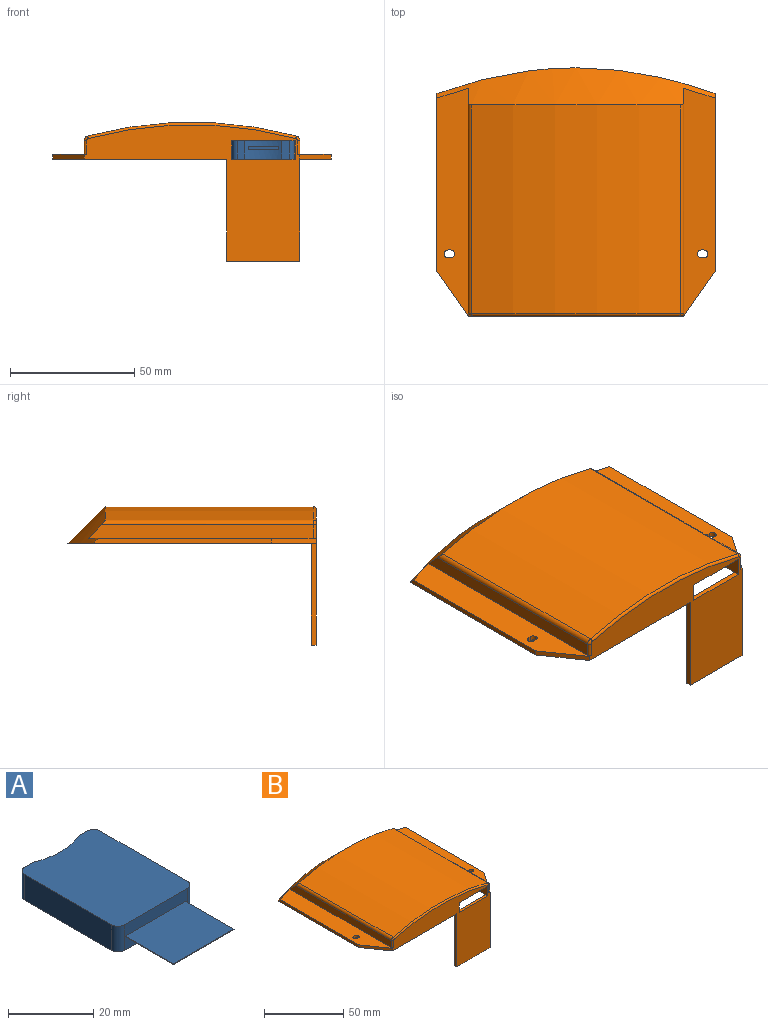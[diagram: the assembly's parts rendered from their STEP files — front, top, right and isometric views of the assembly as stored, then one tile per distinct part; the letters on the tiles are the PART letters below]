
ASSEMBLY  parts=2 mates=1
PART A: 24 faces, bbox 25x49x7.4 mm
  f0: plane 10x1.4mm, normal (1,0,0), area 13.8mm2, adj f5,f14,f15,f16,f17,f18
  f1: plane 10x1.4mm, normal (-1,0,0), area 13.8mm2, adj f5,f14,f15,f16,f17,f18
  f2: plane 29x7.35mm, normal (1,0,0), area 213.2mm2, adj f3,f11,f12,f13
  f3: cylinder r=2mm len=7.35mm, axis (0,0,-1), area 23.1mm2, adj f2,f4,f12,f13
  f4: plane 7.35x3mm, normal (0,1,0), area 22.1mm2, adj f3,f5,f12,f13
  f5: cylinder r=19.5mm len=15mm, axis (0,0,-1), area 96.1mm2, adj f0,f1,f4,f6,f12,f13,f15,f16
  f6: plane 7.35x3mm, normal (0,1,0), area 22.1mm2, adj f5,f7,f12,f13
  f7: cylinder r=2mm len=7.35mm, axis (0,0,-1), area 23.1mm2, adj f6,f8,f12,f13
  f8: plane 29x7.35mm, normal (-1,0,0), area 213.2mm2, adj f7,f9,f12,f13
  f9: cylinder r=2mm len=7.35mm, axis (0,0,-1), area 23.1mm2, adj f8,f10,f12,f13
  f10: plane 21x7.35mm, normal (0,-1,0), area 150.3mm2, adj f9,f11,f12,f13,f19,f20,f21,f23
  f11: cylinder r=2mm len=7.35mm, axis (0,0,-1), area 23.1mm2, adj f2,f10,f12,f13
  f12: plane 33x25mm, normal (0,0,1), area 806.4mm2, adj f2,f3,f4,f5,f6,f7,f8,f9
  f13: plane 33x25mm, normal (0,0,-1), area 806.4mm2, adj f2,f3,f4,f5,f6,f7,f8,f9
  f14: plane 12x1.2mm, normal (0,1,0), area 14.4mm2, adj f0,f1,f15,f17
  f15: plane 12x10mm, normal (0,0,-1), area 112.3mm2, adj f0,f1,f5,f14
  f16: plane 12x9mm, normal (0,0,1), area 100.3mm2, adj f0,f1,f5,f18
  f17: plane 12x1mm, normal (0,0,1), area 12mm2, adj f0,f1,f14,f18
  f18: plane 12x0.2mm, normal (0,1,0), area 2.4mm2, adj f0,f1,f16,f17
  f19: plane 20x15.95mm, normal (0,0,1), area 319.1mm2, adj f10,f20,f21,f22
  f20: plane 15.95x0.2mm, normal (1,0,0), area 3.2mm2, adj f10,f19,f22,f23
  f21: plane 15.95x0.2mm, normal (-1,0,0), area 3.2mm2, adj f10,f19,f22,f23
  f22: plane 20x0.2mm, normal (0,-1,0), area 4mm2, adj f19,f20,f21,f23
  f23: plane 20x15.95mm, normal (0,0,-1), area 319.1mm2, adj f10,f20,f21,f22
PART B: 47 faces, bbox 115.4x100x69.3 mm
  f0: plane 112x100mm, normal (0,0,-1), area 2767mm2, adj f2,f3,f4,f8,f9,f13,f14,f16
  f1: plane 28x3.75mm, normal (0,0,-1), area 59.5mm2, adj f2,f3,f15,f31,f39,f46
  f2: plane 25.5x7.5mm, normal (0,-1,0), area 103.2mm2, adj f0,f1,f15,f16,f17,f39,f40,f41
  f3: plane 27.5x12.38mm, normal (0,1,0), area 196.8mm2, adj f0,f1,f5,f28,f31,f39,f40,f41
  f4: plane 55.5x13mm, normal (0,1,0), area 643.1mm2, adj f0,f5,f29,f31
  f5: cylinder r=159.32mm len=83mm, axis (0,1,0), area 6116.8mm2, adj f3,f4,f28,f29,f30,f31
  f6: plane 91.75x13.5mm, normal (0,0,1), area 999.5mm2, adj f8,f9,f10,f14,f23,f24,f25,f26
  f7: plane 91.75x13.5mm, normal (0,0,1), area 999.5mm2, adj f8,f12,f13,f14,f18,f19,f20,f21
  f8: plane 87x55mm, normal (0,-1,0), area 2050.7mm2, adj f0,f6,f7,f15,f16,f17,f22,f23
  f9: plane 71.65x2mm, normal (1,0,0), area 141.4mm2, adj f0,f6,f14,f23
  f10: plane 90.78x5.53mm, normal (1,0,0), area 484.6mm2, adj f6,f14,f32,f34
  f11: cylinder r=161.32mm len=84.04mm, axis (0,1,0), area 7141.9mm2, adj f14,f32,f33,f36
  f12: plane 90.78x5.53mm, normal (-1,0,0), area 484.6mm2, adj f7,f14,f33,f38
  f13: plane 71.65x2mm, normal (-1,0,0), area 141.4mm2, adj f0,f7,f14,f22
  f14: cone r=161.32mm half-angle=45deg, axis (0,-1,0), area 1671.9mm2, adj f0,f6,f7,f9,f10,f11,f12,f13
  f15: plane 28x7.5mm, normal (1,0,0), area 210mm2, adj f1,f2,f8,f17,f42
  f16: plane 28x7.5mm, normal (-1,0,0), area 210mm2, adj f0,f2,f8,f17,f42
  f17: plane 28x25.5mm, normal (0,0,-1), area 714mm2, adj f2,f8,f15,f16
  f18: plane 2x1mm, normal (0,1,0), area 2mm2, adj f0,f7,f19,f21
  f19: cylinder r=1.6mm len=3.2mm, axis (0,0,-1), area 10.1mm2, adj f0,f7,f18,f20
  f20: plane 2x1mm, normal (0,-1,0), area 2mm2, adj f0,f7,f19,f21
  f21: cylinder r=1.6mm len=3.2mm, axis (0,0,-1), area 10.1mm2, adj f0,f7,f18,f20
  f22: plane 18x12.5mm, normal (-0.82,-0.57,0), area 43.8mm2, adj f0,f7,f8,f13
  f23: plane 18x12.5mm, normal (0.82,-0.57,0), area 43.8mm2, adj f0,f6,f8,f9
  f24: plane 2x1mm, normal (0,-1,0), area 2mm2, adj f0,f6,f25,f27
  f25: cylinder r=1.6mm len=3.2mm, axis (0,0,-1), area 10.1mm2, adj f0,f6,f24,f26
  f26: plane 2x1mm, normal (0,1,0), area 2mm2, adj f0,f6,f25,f27
  f27: cylinder r=1.6mm len=3.2mm, axis (0,0,-1), area 10.1mm2, adj f0,f6,f24,f26
  f28: plane 61.45x7.55mm, normal (-1,0,0), area 433.4mm2, adj f0,f3,f5,f30
  f29: plane 89.45x7.55mm, normal (1,0,0), area 643.4mm2, adj f0,f4,f5,f30
  f30: cone r=159.9mm half-angle=45deg, axis (0,-1,0), area 1312.6mm2, adj f0,f5,f28,f29
  f31: plane 28x12.38mm, normal (-1,0,0), area 346.7mm2, adj f1,f3,f4,f5
  f32: cylinder r=2mm len=85.47mm, axis (0,1,0), area 221mm2, adj f10,f11,f14,f35
  f33: cylinder r=2mm len=85.47mm, axis (0,1,0), area 221mm2, adj f11,f12,f14,f37
  f34: cylinder r=1mm len=5.5mm, axis (0,0,-1), area 8.6mm2, adj f6,f8,f10,f35
  f35: torus R=1mm, axis (0,-1,0), area 3.4mm2, adj f8,f32,f34,f36
  f36: torus R=160.32mm, axis (0,-1,0), area 133.3mm2, adj f8,f11,f35,f37
  f37: torus R=1mm, axis (0,-1,0), area 3.4mm2, adj f8,f33,f36,f38
  f38: cylinder r=1mm len=5.5mm, axis (0,0,1), area 8.6mm2, adj f7,f8,f12,f37
  f39: plane 4x2mm, normal (1,0,0), area 8mm2, adj f1,f2,f3,f41
  f40: plane 4x2mm, normal (-1,0,0), area 8mm2, adj f0,f2,f3,f41
  f41: plane 22x2mm, normal (0,0,-1), area 44mm2, adj f2,f3,f39,f40
  f42: plane 25.5x2mm, normal (0,0,1), area 51mm2, adj f8,f15,f16,f46
  f43: plane 41x2mm, normal (-1,0,0), area 82mm2, adj f0,f8,f44,f46
  f44: plane 29.5x2mm, normal (0,0,-1), area 59mm2, adj f8,f43,f45,f46
  f45: plane 41x2mm, normal (1,0,0), area 82mm2, adj f0,f8,f44,f46
  f46: plane 41x29.5mm, normal (0,1,0), area 1209.5mm2, adj f0,f1,f42,f43,f44,f45
PLACE A rot(axis=(0,0,1),180deg) t=(8.46,-44.75,-3.21)mm
PLACE B t=(-20.29,26.1,-7.03)mm
MATE planar A.f12 <-> B.f17  axis (0,0,1) through (8.46,-44.45,0.47)mm
